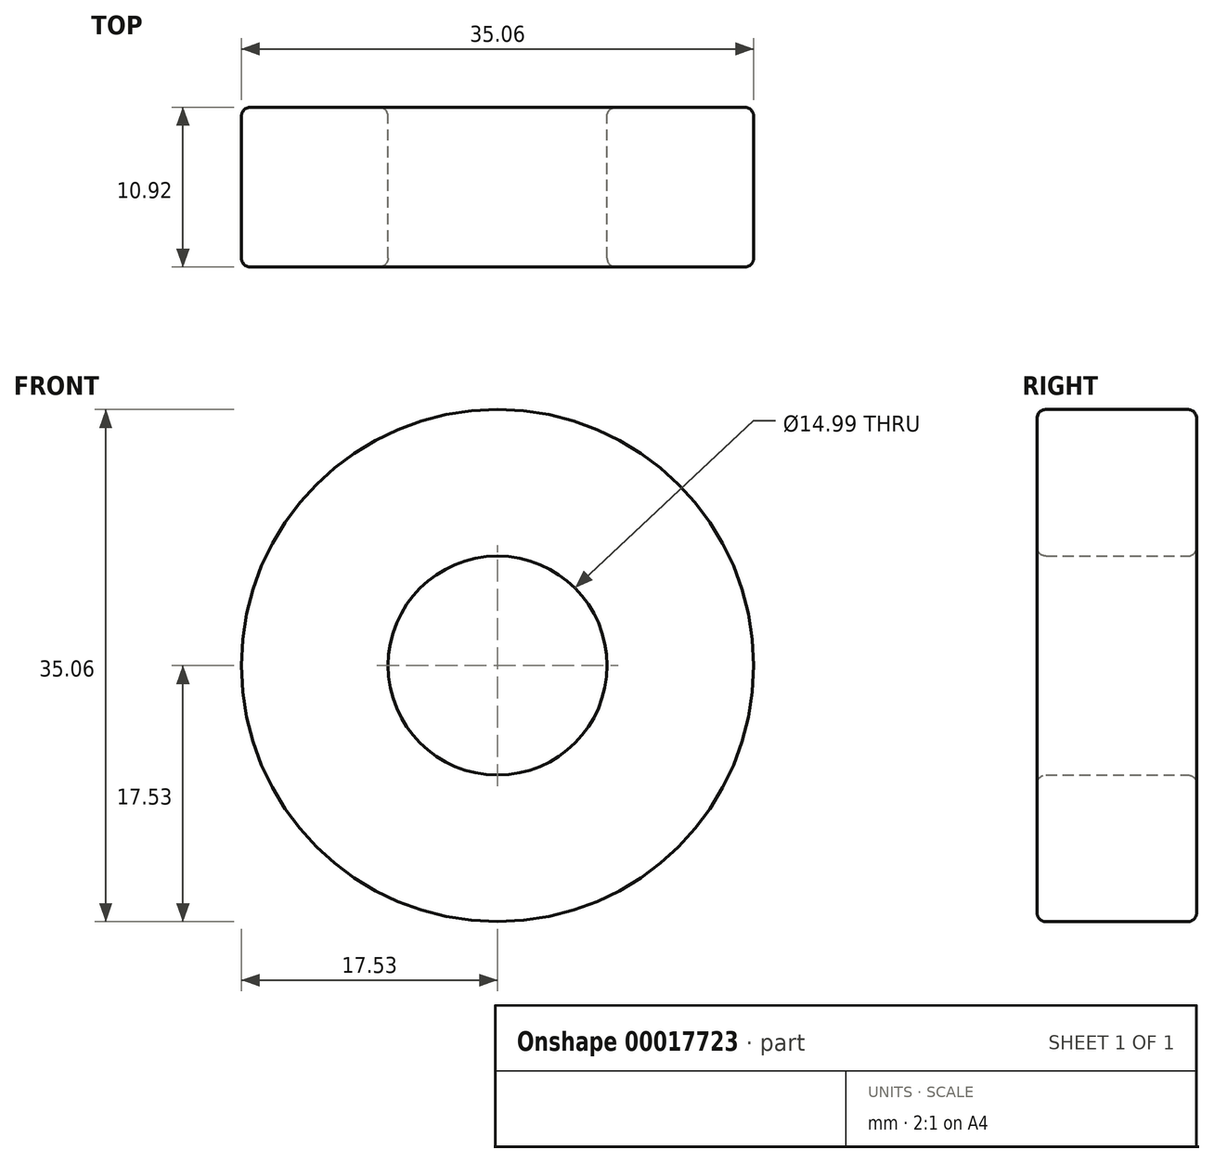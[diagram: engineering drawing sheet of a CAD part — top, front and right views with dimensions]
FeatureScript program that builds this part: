
annotation { "Feature Type Name" : "Feature", "Feature Type Description" : "" }
export const myFeature = defineFeature(function(context is Context, id is Id, definition is map)
    precondition{}
    {
        {
            var Q0;
            Q0=qCreatedBy(makeId("Front.planeOp"),FACE);
            var sketch = newSketch(context, id + "F0", { "sketchPlane" : qUnion([Q0])});
            skCircle(sketch, "E0", {"center": v(0, 0) * mm, "radius": 7.5 * mm});
            skCircle(sketch, "E1", {"center": v(0, 0) * mm, "radius": 17.53 * mm});
            skSolve(sketch);
        }
        {
            var Q0;
            Q0=makeQuery(id+"F0.imprint","IMPRINT",FACE,{"disambiguationData":[TD([[makeQuery(id+"F0.imprint","IMPRINT",EDGE,{"derivedFrom":sQuery(id+"F0.wireOp",EDGE,"E0")}),-1.0]])]});
            extrude(context, id + "F1", {"entities" : qUnion([Q0]), "depth" : 10.92 * mm});
        }
        {
            var Q0;
            Q0=makeQuery(id+"F1.opExtrude","CAP_EDGE",EDGE,{"disambiguationData":[OSD([sQuery(id+"F0.wireOp",EDGE,"E0")])],"isStart":false});
            var Q1;
            Q1=makeQuery(id+"F1.opExtrude","CAP_EDGE",EDGE,{"disambiguationData":[OSD([sQuery(id+"F0.wireOp",EDGE,"E1")])],"isStart":false});
            var Q2;
            Q2=makeQuery(id+"F1.opExtrude","CAP_EDGE",EDGE,{"disambiguationData":[OSD([sQuery(id+"F0.wireOp",EDGE,"E1")])],"isStart":true});
            var Q3;
            Q3=makeQuery(id+"F1.opExtrude","CAP_EDGE",EDGE,{"disambiguationData":[OSD([sQuery(id+"F0.wireOp",EDGE,"E0")])],"isStart":true});
            fillet(context, id + "F2", {"entities" : qUnion([Q0, Q1, Q2, Q3]), "radius" : 0.6 * mm, "tangentPropagation" : true, "allowEdgeOverflow" : false});
        }
    });
